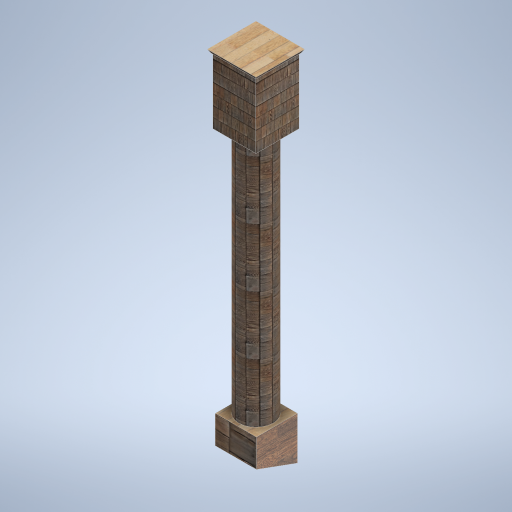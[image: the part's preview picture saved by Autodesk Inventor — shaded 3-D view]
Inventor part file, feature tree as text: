
AUTODESK INVENTOR PART (.ipt)
format: ipt  version: 2024.2 (Build 282272000, 272)  size: 382,464 bytes
history: native  units: mm
features: sketch x5, extrude x4, plane x2
ambient origin geometry x8: Origin, YZ Plane, XZ Plane, XY Plane, X Axis, Y Axis, Z Axis, Center Point
bodies: Solid1 (feature_tree)
feature tree (11):
  sketch  "Sketch1"  dims[d0=239.0mm d2=0.0mm d3=90.0deg]
  plane  "Work Plane3"
  extrude  "Extrusion1"  TaperAngle=0.0deg  [1 undecoded]
  extrude  "Extrusion2"  Depth=3000.0mm
  extrude  "Extrusion3"  Depth=250.0mm
  extrude  "Extrusion4"  Depth=239.0mm
  plane  "Work Plane2"
  sketch  "Sketch2"  dims[d4=3000.0mm d5=3000.0mm]
  sketch  "Sketch3"  dims[d6=3.490659mm d7=250.0mm]
  sketch  "Sketch4"  dims[d8=239.0mm d9=0.0mm d10=200.0mm]
  sketch  "Sketch5"  dims[d11=1431.0mm d12=0.0mm d13=250.0mm d14=250.0mm d15=380.0mm d16=0.0mm d17=260.0mm d18=260.0mm d19=20.0mm d20=30.0deg]
note: 1 required parameter value undecoded (feature->parameter linkage not recoverable at this tier; creation-order binding heuristic only, values carry confidence <= 0.55)
